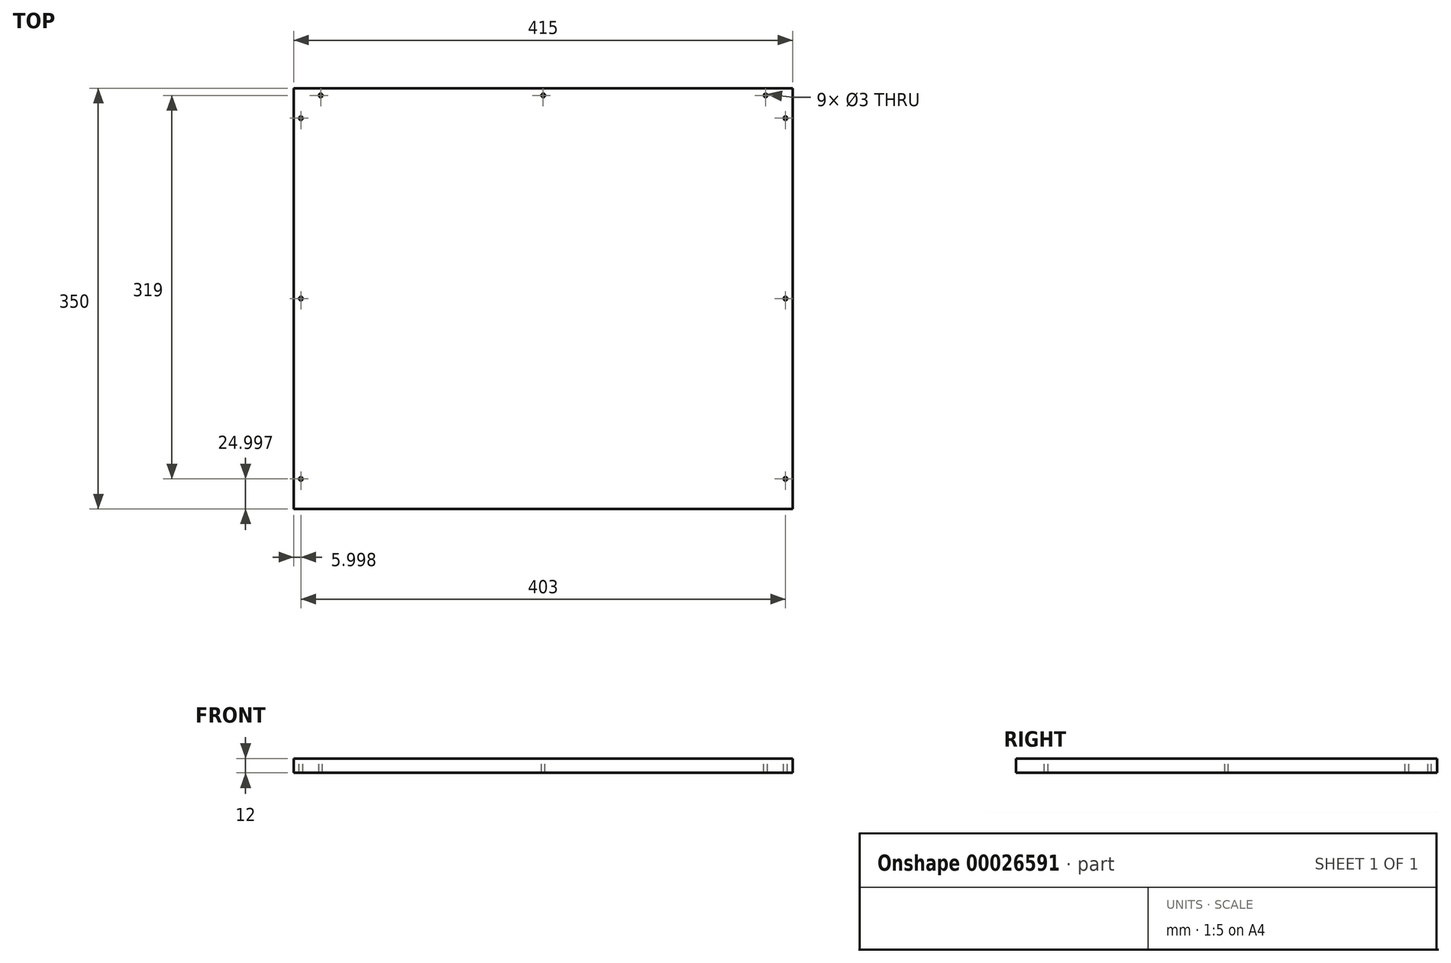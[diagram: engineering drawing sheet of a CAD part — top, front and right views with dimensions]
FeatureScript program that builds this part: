
annotation { "Feature Type Name" : "Feature", "Feature Type Description" : "" }
export const myFeature = defineFeature(function(context is Context, id is Id, definition is map)
    precondition{}
    {
        {
            var Q0;
            Q0=qCreatedBy(makeId("Top.planeOp"),FACE);
            var sketch = newSketch(context, id + "F0", { "sketchPlane" : qUnion([Q0])});
            skLineSegment(sketch, "E0.bottom", {"start": v(-70.96, 65.05) * mm, "end": v(344.04, 65.05) * mm});
            skLineSegment(sketch, "E0.top", {"start": v(-70.96, -284.95) * mm, "end": v(344.04, -284.95) * mm});
            skLineSegment(sketch, "E0.left", {"start": v(-70.96, 65.05) * mm, "end": v(-70.96, -284.95) * mm});
            skLineSegment(sketch, "E0.right", {"start": v(344.04, 65.05) * mm, "end": v(344.04, -284.95) * mm});
            skSolve(sketch);
        }
        {
            var Q0;
            Q0=qSketchRegion(id+"F0",true);
            extrude(context, id + "F1", {"entities" : qUnion([Q0]), "depth" : 12 * mm});
        }
        {
            var Q0;
            Q0=makeQuery(id+"F1.opExtrude","CAP_FACE",FACE,{"disambiguationData":[OSD([sQuery(id+"F0.wireOp",EDGE,"E0.bottom"),sQuery(id+"F0.wireOp",EDGE,"E0.top"),sQuery(id+"F0.wireOp",EDGE,"E0.left"),sQuery(id+"F0.wireOp",EDGE,"E0.right")])],"isStart":false});
            var sketch = newSketch(context, id + "F2", { "sketchPlane" : qUnion([Q0])});
            skCircle(sketch, "E1", {"center": v(-64.96, 40.05) * mm, "radius": 1.5 * mm});
            skCircle(sketch, "E2", {"center": v(-64.96, -109.95) * mm, "radius": 1.5 * mm});
            skCircle(sketch, "E3", {"center": v(-64.96, -259.95) * mm, "radius": 1.5 * mm});
            skLineSegment(sketch, "E4", {"start": v(136.54, 65.05) * mm, "end": v(136.54, -284.95) * mm, "construction": true});
            skCircle(sketch, "E5", {"center": v(-48.46, 59.05) * mm, "radius": 1.5 * mm});
            skLineSegment(sketch, "E6", {"start": v(-70.96, -109.95) * mm, "end": v(136.54, -109.95) * mm, "construction": true});
            skCircle(sketch, "E7", {"center": v(136.54, 59.05) * mm, "radius": 1.5 * mm});
            skCircle(sketch, "E8.MirrorC", {"center": v(338.04, -259.95) * mm, "radius": 1.5 * mm});
            skCircle(sketch, "E9.MirrorC", {"center": v(338.04, 40.05) * mm, "radius": 1.5 * mm});
            skCircle(sketch, "E10.MirrorC", {"center": v(338.04, -109.95) * mm, "radius": 1.5 * mm});
            skCircle(sketch, "E11.MirrorC", {"center": v(321.54, 59.05) * mm, "radius": 1.5 * mm});
            skSolve(sketch);
        }
        {
            var Q0;
            Q0=qSketchRegion(id+"F2",true);
            extrude(context, id + "F3", {"entities" : qUnion([Q0]), "operationType" : NewBodyOperationType.REMOVE, "endBound" : BoundingType.THROUGH_ALL, "oppositeDirection" : true, "depth" : 25 * mm});
        }
    });
